# Revit family: 3890210_3890210C_KON.MAST 10M Ø60 PL200 + Fund. 3520200C
name_source: partatom
category: Lighting Fixtures
units: mm (PartAtom-declared; Revit-internal decimal feet)

## family parameters
Always vertical = Yes
Cut with Voids When Loaded = No
Light Source = No
Maintain Annotation Orientation = No
OmniClass Number = 23.80.70.14.21
OmniClass Title = Street and Roadway Lighting
Part Type = Normal
Room Calculation Point = No
Round Connector Dimension = Use Diameter
Shared = No
Work Plane-Based = No

## types (1)
- Konsike master
    Area = 9,60 m²
    Art.nr = 3790210
    Art.nr CombiCoat = 3890210C
    Art.nr VZN = 3890210
    Bunndiameter = Ø170
    CE-godkjent = Ja
    Category = Konsike master
    Center of Gravity = X: -0,002 mm Y: 0,729 mm Z: 2777,949 mm
    Default Elevation = 0 mm  [stored 0 ft]
    Density = 7859,61 kg/m³
    Description = KON.MAST 10M Ø60 PL200
    Design Status = 1
    EL nr CombiCoat = 3615553
    El nr VZN = 3615545
    Filnamn-VO = Standard
    Filnavn = KON.MAST 10M Ø60 PL200 + Fund. 3520200C
    Fotplate C/C bolter = 200mm
    Fundament = 3520200C
    Lyspunkthoyde = 10m
    Manufacturer = Vik Ørsta AS
    Mass = 118,79 kg
    Model = 3890210_3890210C
    Part Number = L10307
    Requested Accuracy = Low
    Revision Number = -
    Size = 0,0,0
    Sti&Filnamn-VO = Standard
    Title = KON.MAST 10M Ø60 PL200
    Toppdiameter = Ø60
    Volume = 0,02 m³

note: [stored X ft] marks values corroborated as IEEE doubles in the binary element streams (Revit-internal decimal feet)

## geometry (parser evidence)
native form markers: Sweep x3
no freeform markers — native parametric forms only
